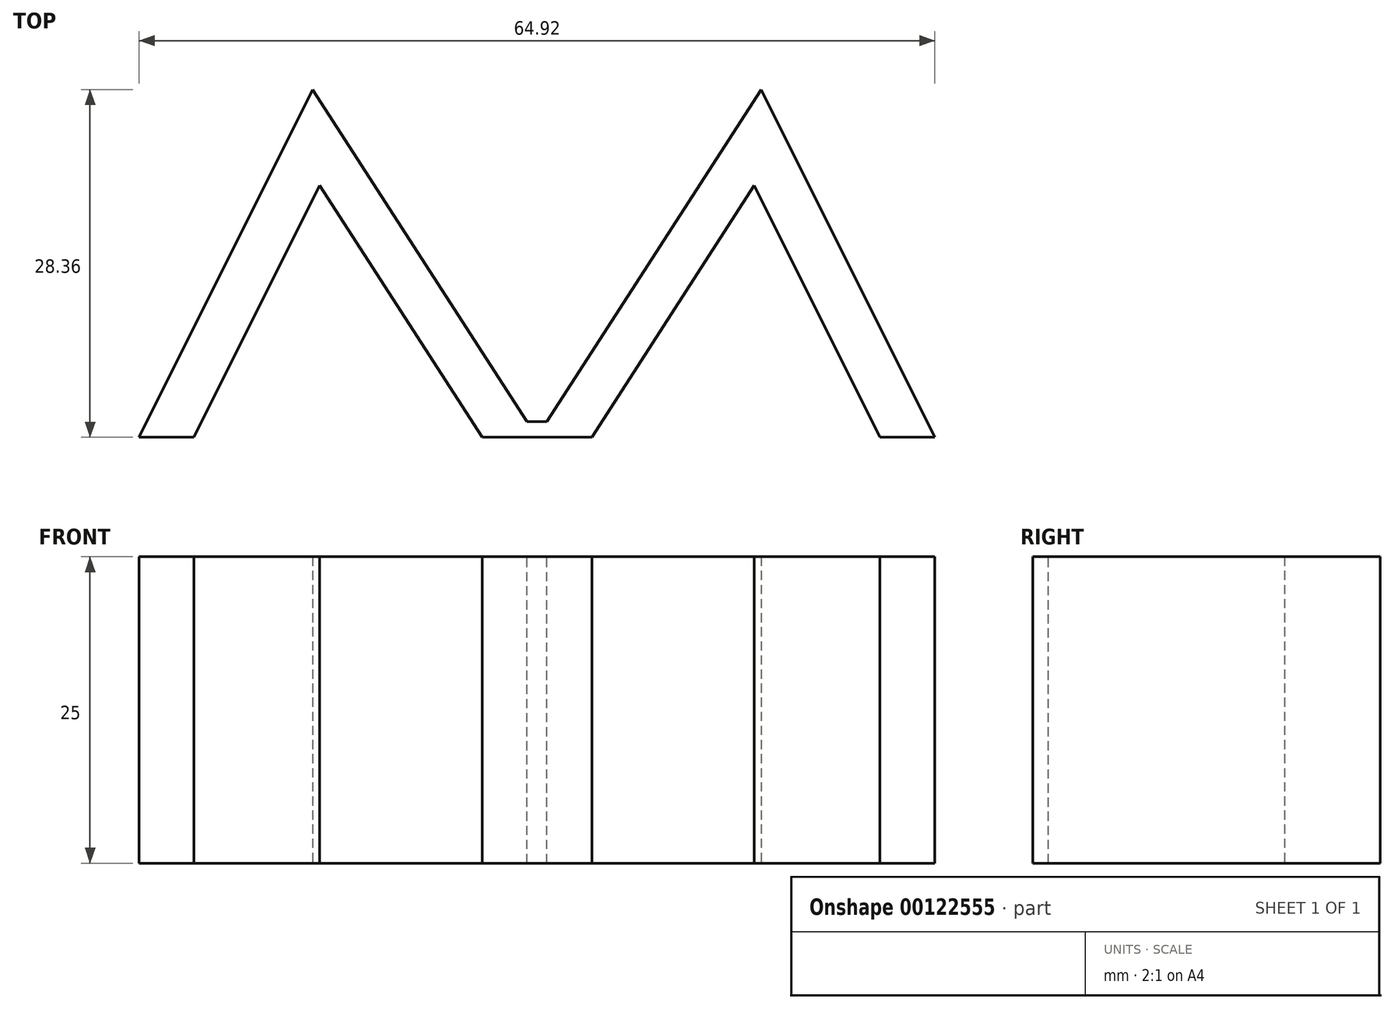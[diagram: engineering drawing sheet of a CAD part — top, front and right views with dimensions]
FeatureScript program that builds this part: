
annotation { "Feature Type Name" : "Feature", "Feature Type Description" : "" }
export const myFeature = defineFeature(function(context is Context, id is Id, definition is map)
    precondition{}
    {
        {
            var Q0;
            Q0=qCreatedBy(makeId("Top.planeOp"),FACE);
            var sketch = newSketch(context, id + "F0", { "sketchPlane" : qUnion([Q0])});
            skLineSegment(sketch, "E0", {"start": v(0, 4) * mm, "end": v(-18.3, 32.36) * mm});
            skLineSegment(sketch, "E1", {"start": v(-17.73, 24.55) * mm, "end": v(-4.47, 4) * mm});
            skLineSegment(sketch, "E2", {"start": v(-4.47, 4) * mm, "end": v(0, 4) * mm});
            skLineSegment(sketch, "E3", {"start": v(-18.3, 32.36) * mm, "end": v(-32.46, 4) * mm});
            skLineSegment(sketch, "E4", {"start": v(-32.46, 4) * mm, "end": v(-28, 4) * mm});
            skLineSegment(sketch, "E5", {"start": v(-28, 4) * mm, "end": v(-17.73, 24.55) * mm});
            skLineSegment(sketch, "E6.MirrorCS", {"start": v(4.47, 4) * mm, "end": v(0, 4) * mm});
            skLineSegment(sketch, "E7.MirrorCS", {"start": v(32.46, 4) * mm, "end": v(28, 4) * mm});
            skLineSegment(sketch, "E8.MirrorCS", {"start": v(28, 4) * mm, "end": v(17.73, 24.55) * mm});
            skLineSegment(sketch, "E9.MirrorCS", {"start": v(18.3, 32.36) * mm, "end": v(32.46, 4) * mm});
            skLineSegment(sketch, "E10.MirrorCS", {"start": v(0, 4) * mm, "end": v(18.3, 32.36) * mm});
            skLineSegment(sketch, "E11.MirrorCS", {"start": v(17.73, 24.55) * mm, "end": v(4.47, 4) * mm});
            skSolve(sketch);
        }
        {
            var Q0;
            Q0 = qSketchRegion(id + "F0", true);
            extrude(context, id + "F1", {"entities" : qUnion([Q0]), "depth" : 25 * mm});
        }
        {
            var Q0;
            Q0=makeQuery(id+"F1.opExtrude","CAP_FACE",FACE,{"disambiguationData":[OSD([sQuery(id+"F0.wireOp",EDGE,"E0"),sQuery(id+"F0.wireOp",EDGE,"E1"),sQuery(id+"F0.wireOp",EDGE,"E2"),sQuery(id+"F0.wireOp",EDGE,"E3"),sQuery(id+"F0.wireOp",EDGE,"E4"),sQuery(id+"F0.wireOp",EDGE,"E5")])],"isStart":false});
            var sketch = newSketch(context, id + "F2", { "sketchPlane" : qUnion([Q0])});
            skPoint(sketch, "E12.0", {"position": v(4.47, 4) * mm});
            skLineSegment(sketch, "E13.bottom", {"start": v(-4.47, 4) * mm, "end": v(4.47, 4) * mm});
            skLineSegment(sketch, "E13.top", {"start": v(-4.47, 5.27) * mm, "end": v(4.47, 5.27) * mm});
            skLineSegment(sketch, "E13.left", {"start": v(-4.47, 4) * mm, "end": v(-4.47, 5.27) * mm});
            skLineSegment(sketch, "E13.right", {"start": v(4.47, 4) * mm, "end": v(4.47, 5.27) * mm});
            skSolve(sketch);
        }
        {
            var Q0;
            Q0 = qSketchRegion(id + "F2", true);
            extrude(context, id + "F3", {"entities" : qUnion([Q0]), "operationType" : NewBodyOperationType.ADD, "oppositeDirection" : true, "depth" : 25 * mm});
        }
    });
